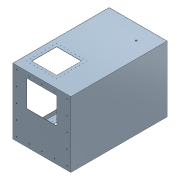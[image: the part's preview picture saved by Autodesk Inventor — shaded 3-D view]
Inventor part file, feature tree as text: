
AUTODESK INVENTOR PART (.ipt)
format: ipt  version: 2017 (Build 210142000, 142)  size: 359,936 bytes
history: native  units: mm
features: extrude x9, sketch x8, fillet x3, hole x2, plane x1
ambient origin geometry x8: Origin, YZ Plane, XZ Plane, XY Plane, X Axis, Y Axis, Z Axis, Center Point
bodies: Solid1 (feature_tree)
feature tree (23):
  extrude  "Extrusion1"  Depth=863.6mm
  extrude  "Extrusion2"  Depth=1270.0mm TaperAngle=0.0deg
  extrude  "Extrusion3"  Depth=3.0mm TaperAngle=0.0deg
  extrude  "Extrusion4"  Depth=3.0mm TaperAngle=0.0deg
  extrude  "Extrusion5"  Depth=330.0mm
  extrude  "Extrusion6"  Depth=150.0mm
  fillet  "Fillet1"  [1 undecoded]
  fillet  "Fillet2"  Radius=35.0mm
  extrude  "Extrusion7"  Depth=5.0mm
  fillet  "Fillet3"  [1 undecoded]
  extrude  "Extrusion8"  Depth=5.0mm
  extrude  "Extrusion9"  Depth=400.0mm
  plane  "Work Plane1"
  hole  "Hole1"  [1 undecoded]
  hole  "Hole2"  [1 undecoded]
  sketch  "Sketch1"  dims[d0=762.0mm d1=863.6mm]
  sketch  "Sketch2"  dims[d2=3.0mm d3=1270.0mm d4=0.0mm]
  sketch  "Sketch3"  dims[d5=3.0mm d6=0.0mm d7=3.0mm d8=0.0mm]
  sketch  "Sketch4"  dims[d9=50.0mm d10=3.0mm d11=0.0mm]
  sketch  "Sketch5"  dims[d12=330.0mm d13=330.0mm]
  sketch  "Sketch7"  dims[d14=100.0mm d15=150.0mm d16=0.0mm d17=0.0mm d18=35.0mm]
  sketch  "Sketch8"  dims[d19=5.0mm d22=61.35mm d48=61.35mm d49=0.0mm]
  sketch  "Sketch10"  dims[d50=5.0mm d51=5.0mm d52=400.0mm d53=350.0mm d54=80.0mm d55=61.35mm d56=0.0mm d57=5.0mm d59=61.35mm d60=0.0mm d91=50.0mm d92=12.0mm d93=90.0mm d95=96.2mm d96=10.0mm d98=10.0mm d100=90.0mm d102=83.5mm d103=10.0mm d105=10.0mm d107=90.0mm d109=83.5mm d110=10.0mm d112=10.0mm d114=80.0mm d116=96.2mm d117=10.0mm d119=10.0mm d121=61.35mm d122=0.0mm d158=90.0mm d160=50.0mm d161=10.0mm d163=10.0mm d165=90.0mm d167=50.0mm d168=10.0mm d170=10.0mm d172=90.0mm d174=50.0mm d175=10.0mm d177=10.0mm d179=80.0mm d181=50.0mm d182=10.0mm d184=10.0mm d186=150.0mm d187=228.0mm d188=80.0mm d189=2.0mm d191=200.0mm d192=210.0mm d193=22.0mm d194=66.498mm d195=34.925mm d196=11.278mm d197=14.3117mm d198=76.498mm d199=20.594885mm d200=80.0mm d201=100.0mm d202=12.0mm d203=6.0mm d204=4.0mm d205=2.0mm d206=90.0deg d207=8.0mm d208=20.594885mm]
note: 4 required parameter values undecoded (feature->parameter linkage not recoverable at this tier; creation-order binding heuristic only, values carry confidence <= 0.55)
